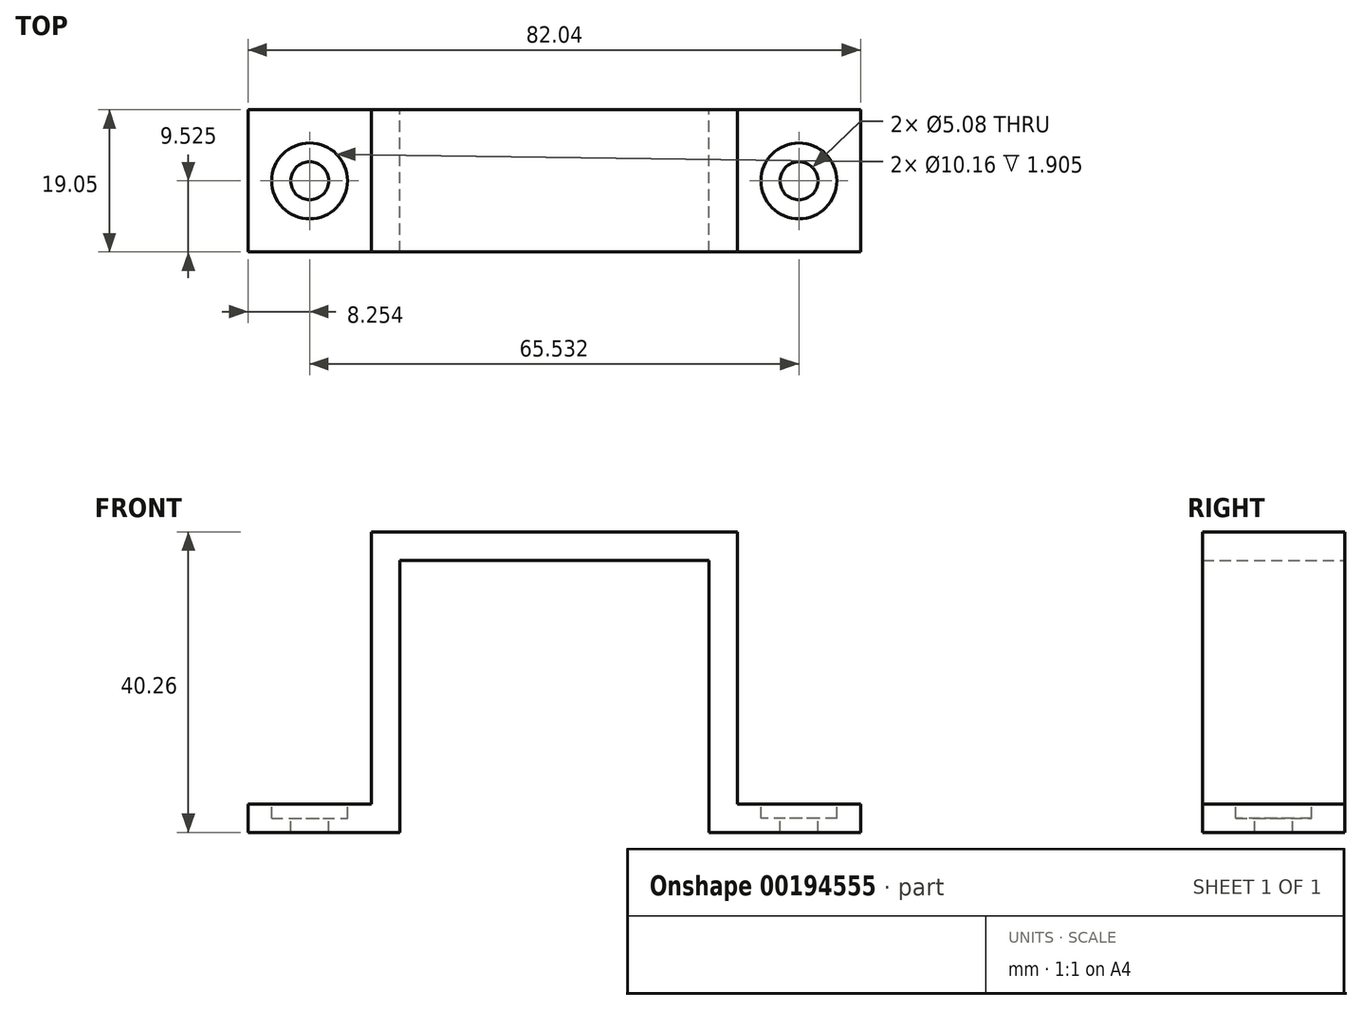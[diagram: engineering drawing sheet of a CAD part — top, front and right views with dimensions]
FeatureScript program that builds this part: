
annotation { "Feature Type Name" : "Feature", "Feature Type Description" : "" }
export const myFeature = defineFeature(function(context is Context, id is Id, definition is map)
    precondition{}
    {
        {
            assignVariable(context, id + "F0", {"name" : "Thickness", "anyValue" : 3.8 * mm});
        }
        {
            var Q0;
            Q0=qCreatedBy(makeId("Front.planeOp"),FACE);
            var sketch = newSketch(context, id + "F1", { "sketchPlane" : qUnion([Q0])});
            skLineSegment(sketch, "E0.right", {"start": v(0, 36.45) * mm, "end": v(0, 40.26) * mm});
            skLineSegment(sketch, "E1.bottom", {"start": v(0, 40.26) * mm, "end": v(24.51, 40.26) * mm});
            skLineSegment(sketch, "E1.top", {"start": v(0, 36.45) * mm, "end": v(24.51, 36.45) * mm});
            skLineSegment(sketch, "E1.left", {"start": v(0, 40.26) * mm, "end": v(0, 36.45) * mm});
            skLineSegment(sketch, "E1.right", {"start": v(24.51, 40.26) * mm, "end": v(24.51, 36.45) * mm});
            skLineSegment(sketch, "E2.bottom", {"start": v(24.51, 40.26) * mm, "end": v(20.7, 40.26) * mm});
            skLineSegment(sketch, "E2.top", {"start": v(24.51, 0) * mm, "end": v(20.7, 0) * mm});
            skLineSegment(sketch, "E2.left", {"start": v(24.51, 40.26) * mm, "end": v(24.51, 0) * mm});
            skLineSegment(sketch, "E2.right", {"start": v(20.7, 40.26) * mm, "end": v(20.7, 0) * mm});
            skLineSegment(sketch, "E3.bottom", {"start": v(20.7, 0) * mm, "end": v(41.02, 0) * mm});
            skLineSegment(sketch, "E3.top", {"start": v(20.7, 3.8) * mm, "end": v(41.02, 3.8) * mm});
            skLineSegment(sketch, "E3.left", {"start": v(20.7, 0) * mm, "end": v(20.7, 3.8) * mm});
            skLineSegment(sketch, "E3.right", {"start": v(41.02, 0) * mm, "end": v(41.02, 3.8) * mm});
            skSolve(sketch);
        }
        {
            var Q0;
            Q0 = qSketchRegion(id + "F1", true);
            extrude(context, id + "F2", {"entities" : qUnion([Q0]), "depth" : 19.05 * mm});
        }
        {
            var Q0;
            Q0=makeQuery(id+"F2.opExtrude","SWEPT_FACE",FACE,{"disambiguationData":[OSD([sQuery(id+"F1.wireOp",EDGE,"E3.top")])]});
            var sketch = newSketch(context, id + "F3", { "sketchPlane" : qUnion([Q0])});
            skCircle(sketch, "E4", {"center": v(32.77, -9.53) * mm, "radius": 2.54 * mm});
            skLineSegment(sketch, "E5", {"start": v(32.77, 0) * mm, "end": v(32.77, -9.53) * mm, "construction": true});
            skLineSegment(sketch, "E6", {"start": v(32.77, -9.53) * mm, "end": v(32.77, -19.05) * mm, "construction": true});
            skLineSegment(sketch, "E7", {"start": v(41.02, -9.53) * mm, "end": v(32.77, -9.53) * mm, "construction": true});
            skLineSegment(sketch, "E8", {"start": v(24.51, -9.53) * mm, "end": v(32.77, -9.53) * mm, "construction": true});
            skSolve(sketch);
        }
        {
            var Q0;
            Q0 = qSketchRegion(id + "F3", true);
            extrude(context, id + "F4", {"entities" : qUnion([Q0]), "operationType" : NewBodyOperationType.REMOVE, "endBound" : BoundingType.THROUGH_ALL, "oppositeDirection" : true, "depth" : 25.4 * mm});
        }
        {
            var Q0;
            Q0=makeQuery(id+"F2.opExtrude","SWEPT_FACE",FACE,{"disambiguationData":[OSD([sQuery(id+"F1.wireOp",EDGE,"E3.top")])]});
            var sketch = newSketch(context, id + "F5", { "sketchPlane" : qUnion([Q0])});
            skCircle(sketch, "E9", {"center": v(32.77, -9.53) * mm, "radius": 5.08 * mm});
            skLineSegment(sketch, "E10", {"start": v(32.77, 0) * mm, "end": v(32.77, -9.53) * mm, "construction": true});
            skLineSegment(sketch, "E11", {"start": v(32.77, -9.53) * mm, "end": v(32.77, -19.05) * mm, "construction": true});
            skLineSegment(sketch, "E12", {"start": v(41.02, -9.53) * mm, "end": v(32.77, -9.53) * mm, "construction": true});
            skLineSegment(sketch, "E13", {"start": v(24.51, -9.53) * mm, "end": v(32.77, -9.53) * mm, "construction": true});
            skSolve(sketch);
        }
        {
            var Q0;
            Q0 = qSketchRegion(id + "F5", true);
            extrude(context, id + "F6", {"entities" : qUnion([Q0]), "operationType" : NewBodyOperationType.REMOVE, "oppositeDirection" : true, "depth" : getVariable(context, 'Thickness') / 2});
        }
        {
            var Q0;
            Q0=makeQuery(id+"F2.opExtrude","SWEPT_BODY",BODY,{"disambiguationData":[OSD([sQuery(id+"F1.wireOp",EDGE,"E1.bottom"),sQuery(id+"F1.wireOp",EDGE,"E1.top"),sQuery(id+"F1.wireOp",EDGE,"E1.left"),sQuery(id+"F1.wireOp",EDGE,"E2.bottom"),sQuery(id+"F1.wireOp",EDGE,"E2.left"),sQuery(id+"F1.wireOp",EDGE,"E2.right"),sQuery(id+"F1.wireOp",EDGE,"E3.bottom"),sQuery(id+"F1.wireOp",EDGE,"E3.top"),sQuery(id+"F1.wireOp",EDGE,"E3.left"),sQuery(id+"F1.wireOp",EDGE,"E3.right")])]});
            var Q1;
            Q1=qCreatedBy(makeId("Right.planeOp"),FACE);
            mirror(context, id + "F7", {"operationType" : NewBodyOperationType.ADD, "entities" : qUnion([Q0]), "mirrorPlane" : qUnion([Q1])});
        }
    });
